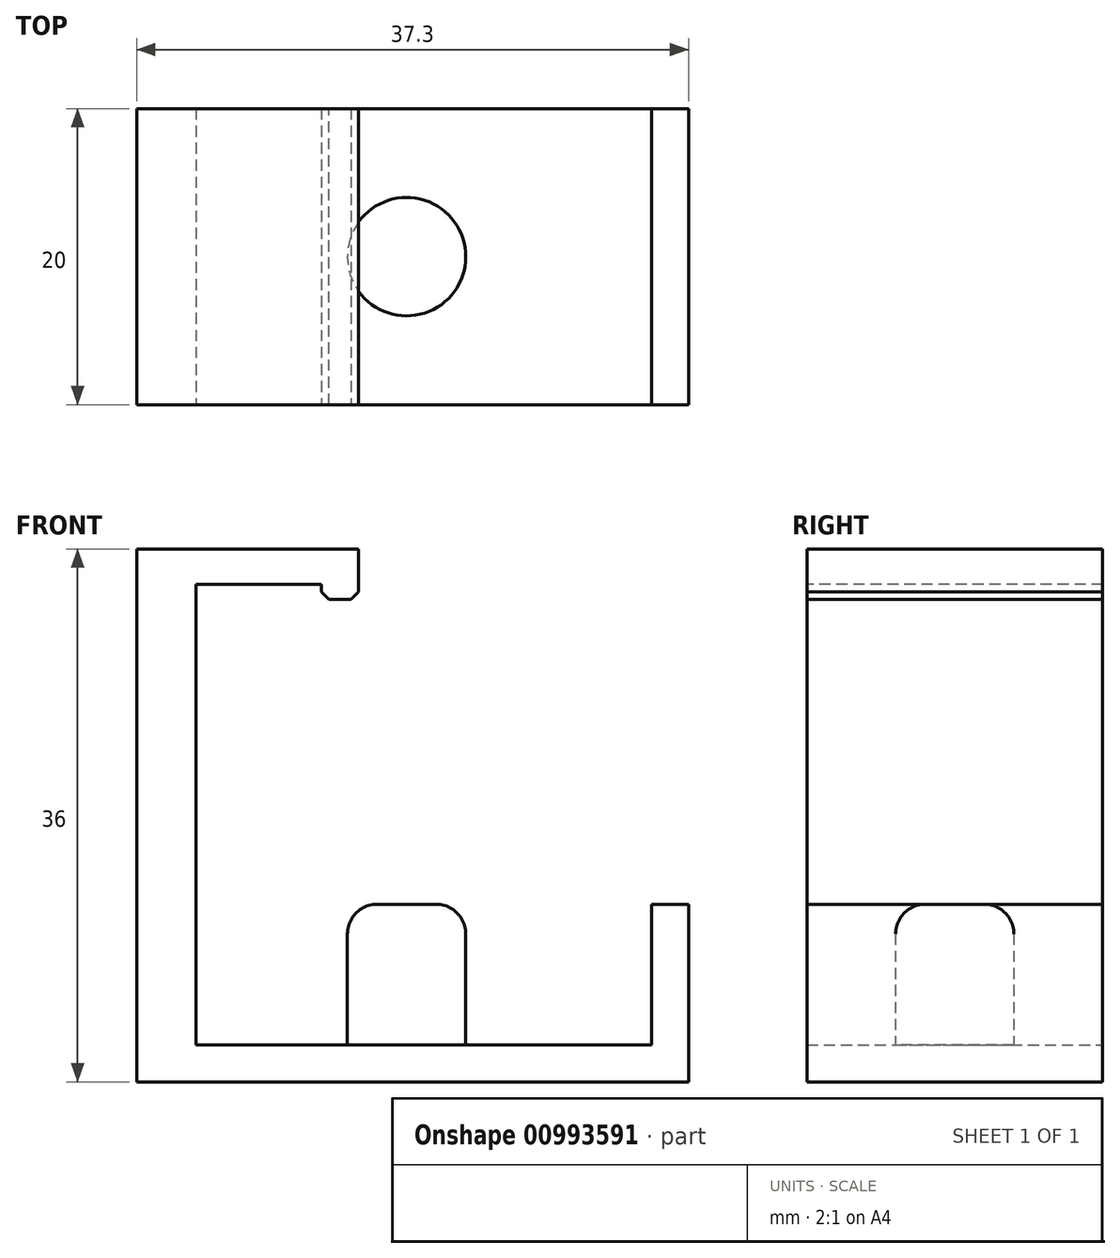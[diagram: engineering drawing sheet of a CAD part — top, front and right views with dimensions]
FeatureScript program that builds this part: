
annotation { "Feature Type Name" : "Feature", "Feature Type Description" : "" }
export const myFeature = defineFeature(function(context is Context, id is Id, definition is map)
    precondition{}
    {
        {
            var Q0;
            Q0=qCreatedBy(makeId("Top.planeOp"),FACE);
            var sketch = newSketch(context, id + "F0", { "sketchPlane" : qUnion([Q0])});
            skCircle(sketch, "E0", {"center": v(-37.39, 16.25) * mm, "radius": 4 * mm});
            skLineSegment(sketch, "E1.bottom", {"start": v(-55.63, 26.25) * mm, "end": v(-18.33, 26.25) * mm});
            skLineSegment(sketch, "E1.top", {"start": v(-55.63, 6.25) * mm, "end": v(-18.33, 6.25) * mm});
            skLineSegment(sketch, "E1.left", {"start": v(-55.63, 26.25) * mm, "end": v(-55.63, 6.25) * mm});
            skLineSegment(sketch, "E1.right", {"start": v(-18.33, 26.25) * mm, "end": v(-18.33, 6.25) * mm});
            skLineSegment(sketch, "E2", {"start": v(-51.63, 26.25) * mm, "end": v(-51.63, 6.25) * mm});
            skLineSegment(sketch, "E3", {"start": v(-20.83, 26.25) * mm, "end": v(-20.83, 6.25) * mm});
            skLineSegment(sketch, "E4", {"start": v(-40.63, 26.25) * mm, "end": v(-40.63, 6.25) * mm});
            skLineSegment(sketch, "E5", {"start": v(-43.13, 26.25) * mm, "end": v(-43.13, 6.25) * mm});
            skSolve(sketch);
        }
        {
            var Q0;
            Q0=makeQuery(id+"F0.imprint","IMPRINT",FACE,{"disambiguationData":[TD([[makeQuery(id+"F0.imprint","IMPRINT",EDGE,{"derivedFrom":sQuery(id+"F0.wireOp",EDGE,"E0")}),-1.0]])]});
            var Q1;
            Q1=makeQuery(id+"F0.imprint","IMPRINT",FACE,{"disambiguationData":[TD([[makeQuery(id+"F0.imprint","IMPRINT",EDGE,{"derivedFrom":sQuery(id+"F0.wireOp",EDGE,"E0")}),1.0]])]});
            var Q2;
            {var subQ0=sQuery(id+"F0.wireOp",EDGE,"E1.right");Q2=makeQuery(id+"F0.imprint","IMPRINT",FACE,{"disambiguationData":[TD([[makeQuery(id+"F0.imprint","IMPRINT",EDGE,{"derivedFrom":subQ0}),-1.0]])]});}
            var Q3;
            {var subQ0=sQuery(id+"F0.wireOp",EDGE,"E1.left");Q3=makeQuery(id+"F0.imprint","IMPRINT",FACE,{"disambiguationData":[TD([[makeQuery(id+"F0.imprint","IMPRINT",EDGE,{"derivedFrom":subQ0}),1.0]])]});}
            var Q4;
            {var subQ0=sQuery(id+"F0.wireOp",EDGE,"E2");Q4=makeQuery(id+"F0.imprint","IMPRINT",FACE,{"disambiguationData":[TD([[makeQuery(id+"F0.imprint","IMPRINT",EDGE,{"derivedFrom":subQ0}),1.0]])]});}
            extrude(context, id + "F1", {"entities" : qUnion([Q0, Q1, Q2, Q3, Q4]), "depth" : 2.5 * mm, "offsetDistance" : 25 * mm});
        }
        {
            var Q0;
            {var subQ0=sQuery(id+"F0.wireOp",EDGE,"E1.right");Q0=makeQuery(id+"F0.imprint","IMPRINT",FACE,{"disambiguationData":[TD([[makeQuery(id+"F0.imprint","IMPRINT",EDGE,{"derivedFrom":subQ0}),-1.0]])]});}
            extrude(context, id + "F2", {"entities" : qUnion([Q0]), "operationType" : NewBodyOperationType.ADD, "depth" : 12 * mm, "offsetDistance" : 25 * mm});
        }
        {
            var Q0;
            Q0=makeQuery(id+"F0.imprint","IMPRINT",FACE,{"disambiguationData":[TD([[makeQuery(id+"F0.imprint","IMPRINT",EDGE,{"derivedFrom":sQuery(id+"F0.wireOp",EDGE,"E0")}),1.0]])]});
            extrude(context, id + "F3", {"entities" : qUnion([Q0]), "operationType" : NewBodyOperationType.ADD, "depth" : 12 * mm, "offsetDistance" : 25 * mm});
        }
        {
            var Q0;
            {var subQ0=sQuery(id+"F0.wireOp",EDGE,"E1.left");Q0=makeQuery(id+"F0.imprint","IMPRINT",FACE,{"disambiguationData":[TD([[makeQuery(id+"F0.imprint","IMPRINT",EDGE,{"derivedFrom":subQ0}),1.0]])]});}
            extrude(context, id + "F4", {"entities" : qUnion([Q0]), "operationType" : NewBodyOperationType.ADD, "depth" : 36 * mm, "offsetDistance" : 25 * mm});
        }
        {
            var Q0;
            {var subQ0=sQuery(id+"F0.wireOp",EDGE,"E2");Q0=makeQuery(id+"F0.imprint","IMPRINT",FACE,{"disambiguationData":[TD([[makeQuery(id+"F0.imprint","IMPRINT",EDGE,{"derivedFrom":subQ0}),1.0]])]});}
            extrude(context, id + "F5", {"entities" : qUnion([Q0]), "operationType" : NewBodyOperationType.ADD, "depth" : 36 * mm, "offsetDistance" : 25 * mm, "hasSecondDirection" : true, "secondDirectionOppositeDirection" : false, "secondDirectionDepth" : 33.6 * mm});
        }
        {
            var Q0;
            Q0=makeQuery(id+"F3.opExtrude","CAP_EDGE",EDGE,{"disambiguationData":[OSD([sQuery(id+"F0.wireOp",EDGE,"E0")])],"isStart":false});
            fillet(context, id + "F6", {"entities" : qUnion([Q0]), "radius" : 2 * mm, "tangentPropagation" : true, "allowEdgeOverflow" : false});
        }
        {
            var Q0;
            {var subQ7=sQuery(id+"F0.wireOp",EDGE,"E5");Q0=makeQuery(id+"F0.imprint","IMPRINT",FACE,{"disambiguationData":[TD([[makeQuery(id+"F0.imprint","IMPRINT",EDGE,{"derivedFrom":subQ7}),1.0]])]});}
            var Q1;
            {var subQ0=sQuery(id+"F0.wireOp",EDGE,"E4");var subQ1=sQuery(id+"F0.wireOp",EDGE,"E0");var subQ2=makeQuery(id+"F0.imprint","INTERSECT",VERTEX,{"disambiguationData":[OD(0.0)],"derivedFrom":[subQ1,subQ0]});Q1=makeQuery(id+"F0.imprint","IMPRINT",FACE,{"disambiguationData":[TD([[makeQuery(id+"F0.imprint","IMPRINT",EDGE,{"disambiguationData":[TD([[subQ2,-1.0]])],"derivedFrom":subQ1}),1.0]])]});}
            extrude(context, id + "F7", {"entities" : qUnion([Q0, Q1]), "operationType" : NewBodyOperationType.ADD, "depth" : 36 * mm, "offsetDistance" : 25 * mm, "hasSecondDirection" : true, "secondDirectionOppositeDirection" : false, "secondDirectionDepth" : 32.6 * mm});
        }
        {
            var Q0;
            Q0=makeQuery(id+"F7.opExtrude","CAP_EDGE",EDGE,{"disambiguationData":[OSD([sQuery(id+"F0.wireOp",EDGE,"E4")])],"isStart":true});
            var Q1;
            Q1=makeQuery(id+"F7.opExtrude","CAP_EDGE",EDGE,{"disambiguationData":[OSD([sQuery(id+"F0.wireOp",EDGE,"E5")])],"isStart":true});
            chamfer(context, id + "F8", {"entities" : qUnion([Q0, Q1]), "width" : .5 * mm, "tangentPropagation" : true});
        }
    });
